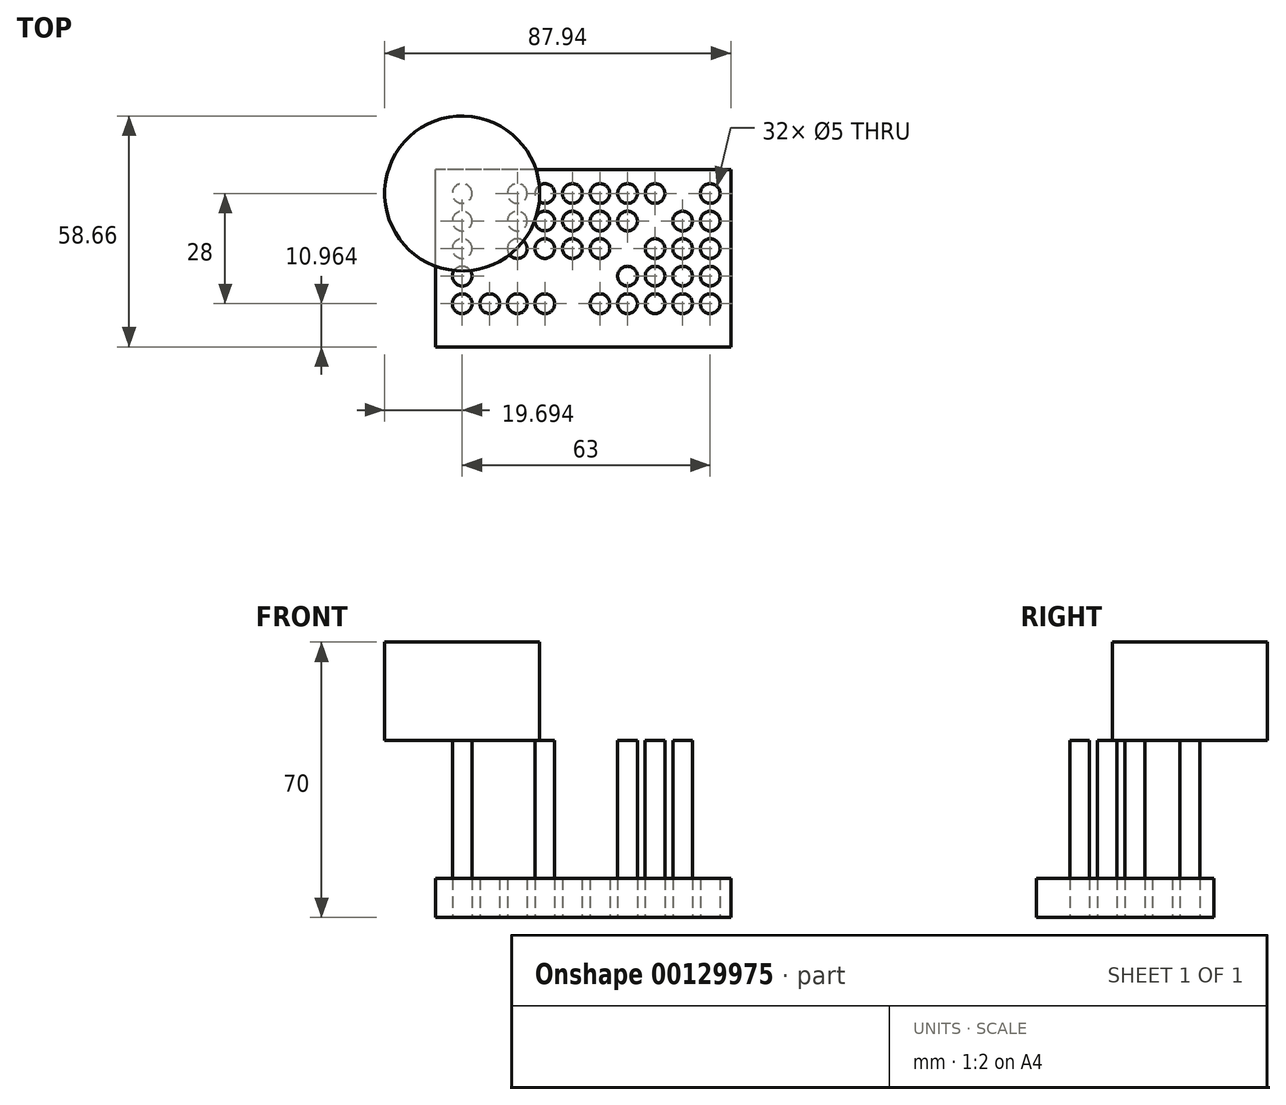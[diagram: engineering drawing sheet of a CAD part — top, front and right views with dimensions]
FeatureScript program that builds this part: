
annotation { "Feature Type Name" : "Feature", "Feature Type Description" : "" }
export const myFeature = defineFeature(function(context is Context, id is Id, definition is map)
    precondition{}
    {
        {
            var Q0;
            Q0=qCreatedBy(makeId("Top.planeOp"),FACE);
            var sketch = newSketch(context, id + "F0", { "sketchPlane" : qUnion([Q0])});
            skLineSegment(sketch, "E0.bottom", {"start": v(37.5, -22.5) * mm, "end": v(-37.5, -22.5) * mm});
            skLineSegment(sketch, "E0.top", {"start": v(37.5, 22.5) * mm, "end": v(-37.5, 22.5) * mm});
            skLineSegment(sketch, "E0.left", {"start": v(37.5, -22.5) * mm, "end": v(37.5, 22.5) * mm});
            skLineSegment(sketch, "E0.right", {"start": v(-37.5, -22.5) * mm, "end": v(-37.5, 22.5) * mm});
            skPoint(sketch, "E0.middle", {"position": v(0, 0) * mm});
            skCircle(sketch, "E1", {"center": v(-30.75, 16.46) * mm, "radius": 2.5 * mm});
            skCircle(sketch, "E2.0.1.0", {"center": v(-30.75, 9.46) * mm, "radius": 2.5 * mm});
            skCircle(sketch, "E2.0.2.0", {"center": v(-30.75, 2.46) * mm, "radius": 2.5 * mm});
            skCircle(sketch, "E2.0.3.0", {"center": v(-30.75, -4.54) * mm, "radius": 2.5 * mm});
            skCircle(sketch, "E2.0.4.0", {"center": v(-30.75, -11.54) * mm, "radius": 2.5 * mm});
            skCircle(sketch, "E2.1.0.0", {"center": v(-23.75, 16.46) * mm, "radius": 2.5 * mm});
            skCircle(sketch, "E2.1.1.0", {"center": v(-23.75, 9.46) * mm, "radius": 2.5 * mm});
            skCircle(sketch, "E2.1.2.0", {"center": v(-23.75, 2.46) * mm, "radius": 2.5 * mm});
            skCircle(sketch, "E2.1.3.0", {"center": v(-23.75, -4.54) * mm, "radius": 2.5 * mm});
            skCircle(sketch, "E2.1.4.0", {"center": v(-23.75, -11.54) * mm, "radius": 2.5 * mm});
            skCircle(sketch, "E2.2.0.0", {"center": v(-16.75, 16.46) * mm, "radius": 2.5 * mm});
            skCircle(sketch, "E2.2.1.0", {"center": v(-16.75, 9.46) * mm, "radius": 2.5 * mm});
            skCircle(sketch, "E2.2.2.0", {"center": v(-16.75, 2.46) * mm, "radius": 2.5 * mm});
            skCircle(sketch, "E2.2.3.0", {"center": v(-16.75, -4.54) * mm, "radius": 2.5 * mm});
            skCircle(sketch, "E2.2.4.0", {"center": v(-16.75, -11.54) * mm, "radius": 2.5 * mm});
            skCircle(sketch, "E2.3.0.0", {"center": v(-9.75, 16.46) * mm, "radius": 2.5 * mm});
            skCircle(sketch, "E2.3.1.0", {"center": v(-9.75, 9.46) * mm, "radius": 2.5 * mm});
            skCircle(sketch, "E2.3.2.0", {"center": v(-9.75, 2.46) * mm, "radius": 2.5 * mm});
            skCircle(sketch, "E2.3.3.0", {"center": v(-9.75, -4.54) * mm, "radius": 2.5 * mm});
            skCircle(sketch, "E2.3.4.0", {"center": v(-9.75, -11.54) * mm, "radius": 2.5 * mm});
            skCircle(sketch, "E2.4.0.0", {"center": v(-2.75, 16.46) * mm, "radius": 2.5 * mm});
            skCircle(sketch, "E2.4.1.0", {"center": v(-2.75, 9.46) * mm, "radius": 2.5 * mm});
            skCircle(sketch, "E2.4.2.0", {"center": v(-2.75, 2.46) * mm, "radius": 2.5 * mm});
            skCircle(sketch, "E2.4.3.0", {"center": v(-2.75, -4.54) * mm, "radius": 2.5 * mm});
            skCircle(sketch, "E2.4.4.0", {"center": v(-2.75, -11.54) * mm, "radius": 2.5 * mm});
            skCircle(sketch, "E2.5.0.0", {"center": v(4.25, 16.46) * mm, "radius": 2.5 * mm});
            skCircle(sketch, "E2.5.1.0", {"center": v(4.25, 9.46) * mm, "radius": 2.5 * mm});
            skCircle(sketch, "E2.5.2.0", {"center": v(4.25, 2.46) * mm, "radius": 2.5 * mm});
            skCircle(sketch, "E2.5.3.0", {"center": v(4.25, -4.54) * mm, "radius": 2.5 * mm});
            skCircle(sketch, "E2.5.4.0", {"center": v(4.25, -11.54) * mm, "radius": 2.5 * mm});
            skCircle(sketch, "E2.6.0.0", {"center": v(11.25, 16.46) * mm, "radius": 2.5 * mm});
            skCircle(sketch, "E2.6.1.0", {"center": v(11.25, 9.46) * mm, "radius": 2.5 * mm});
            skCircle(sketch, "E2.6.2.0", {"center": v(11.25, 2.46) * mm, "radius": 2.5 * mm});
            skCircle(sketch, "E2.6.3.0", {"center": v(11.25, -4.54) * mm, "radius": 2.5 * mm});
            skCircle(sketch, "E2.6.4.0", {"center": v(11.25, -11.54) * mm, "radius": 2.5 * mm});
            skCircle(sketch, "E2.7.0.0", {"center": v(18.25, 16.46) * mm, "radius": 2.5 * mm});
            skCircle(sketch, "E2.7.1.0", {"center": v(18.25, 9.46) * mm, "radius": 2.5 * mm});
            skCircle(sketch, "E2.7.2.0", {"center": v(18.25, 2.46) * mm, "radius": 2.5 * mm});
            skCircle(sketch, "E2.7.3.0", {"center": v(18.25, -4.54) * mm, "radius": 2.5 * mm});
            skCircle(sketch, "E2.7.4.0", {"center": v(18.25, -11.54) * mm, "radius": 2.5 * mm});
            skCircle(sketch, "E2.8.0.0", {"center": v(25.25, 16.46) * mm, "radius": 2.5 * mm});
            skCircle(sketch, "E2.8.1.0", {"center": v(25.25, 9.46) * mm, "radius": 2.5 * mm});
            skCircle(sketch, "E2.8.2.0", {"center": v(25.25, 2.46) * mm, "radius": 2.5 * mm});
            skCircle(sketch, "E2.8.3.0", {"center": v(25.25, -4.54) * mm, "radius": 2.5 * mm});
            skCircle(sketch, "E2.8.4.0", {"center": v(25.25, -11.54) * mm, "radius": 2.5 * mm});
            skCircle(sketch, "E2.9.0.0", {"center": v(32.25, 16.46) * mm, "radius": 2.5 * mm});
            skCircle(sketch, "E2.9.1.0", {"center": v(32.25, 9.46) * mm, "radius": 2.5 * mm});
            skCircle(sketch, "E2.9.2.0", {"center": v(32.25, 2.46) * mm, "radius": 2.5 * mm});
            skCircle(sketch, "E2.9.3.0", {"center": v(32.25, -4.54) * mm, "radius": 2.5 * mm});
            skCircle(sketch, "E2.9.4.0", {"center": v(32.25, -11.54) * mm, "radius": 2.5 * mm});
            skLineSegment(sketch, "E2.direction1", {"start": v(-30.75, 16.46) * mm, "end": v(-23.75, 16.46) * mm, "construction": true});
            skLineSegment(sketch, "E2.direction2", {"start": v(-30.75, 16.46) * mm, "end": v(-30.75, 9.46) * mm, "construction": true});
            skSolve(sketch);
        }
        {
            var Q0;
            Q0 = qSketchRegion(id + "F0", true);
            var Q1;
            Q1=makeQuery(id+"F0.imprint","IMPRINT",FACE,{"disambiguationData":[TD([[makeQuery(id+"F0.imprint","IMPRINT",EDGE,{"derivedFrom":sQuery(id+"F0.wireOp",EDGE,"E2.1.0.0")}),1.0]])]});
            var Q2;
            Q2=makeQuery(id+"F0.imprint","IMPRINT",FACE,{"disambiguationData":[TD([[makeQuery(id+"F0.imprint","IMPRINT",EDGE,{"derivedFrom":sQuery(id+"F0.wireOp",EDGE,"E2.1.1.0")}),1.0]])]});
            var Q3;
            Q3=makeQuery(id+"F0.imprint","IMPRINT",FACE,{"disambiguationData":[TD([[makeQuery(id+"F0.imprint","IMPRINT",EDGE,{"derivedFrom":sQuery(id+"F0.wireOp",EDGE,"E2.1.2.0")}),1.0]])]});
            var Q4;
            Q4=makeQuery(id+"F0.imprint","IMPRINT",FACE,{"disambiguationData":[TD([[makeQuery(id+"F0.imprint","IMPRINT",EDGE,{"derivedFrom":sQuery(id+"F0.wireOp",EDGE,"E2.1.3.0")}),1.0]])]});
            var Q5;
            Q5=makeQuery(id+"F0.imprint","IMPRINT",FACE,{"disambiguationData":[TD([[makeQuery(id+"F0.imprint","IMPRINT",EDGE,{"derivedFrom":sQuery(id+"F0.wireOp",EDGE,"E2.2.3.0")}),1.0]])]});
            var Q6;
            Q6=makeQuery(id+"F0.imprint","IMPRINT",FACE,{"disambiguationData":[TD([[makeQuery(id+"F0.imprint","IMPRINT",EDGE,{"derivedFrom":sQuery(id+"F0.wireOp",EDGE,"E2.3.3.0")}),1.0]])]});
            var Q7;
            Q7=makeQuery(id+"F0.imprint","IMPRINT",FACE,{"disambiguationData":[TD([[makeQuery(id+"F0.imprint","IMPRINT",EDGE,{"derivedFrom":sQuery(id+"F0.wireOp",EDGE,"E2.4.3.0")}),1.0]])]});
            var Q8;
            Q8=makeQuery(id+"F0.imprint","IMPRINT",FACE,{"disambiguationData":[TD([[makeQuery(id+"F0.imprint","IMPRINT",EDGE,{"derivedFrom":sQuery(id+"F0.wireOp",EDGE,"E2.4.4.0")}),1.0]])]});
            var Q9;
            Q9=makeQuery(id+"F0.imprint","IMPRINT",FACE,{"disambiguationData":[TD([[makeQuery(id+"F0.imprint","IMPRINT",EDGE,{"derivedFrom":sQuery(id+"F0.wireOp",EDGE,"E2.5.3.0")}),1.0]])]});
            var Q10;
            Q10=makeQuery(id+"F0.imprint","IMPRINT",FACE,{"disambiguationData":[TD([[makeQuery(id+"F0.imprint","IMPRINT",EDGE,{"derivedFrom":sQuery(id+"F0.wireOp",EDGE,"E2.6.2.0")}),1.0]])]});
            var Q11;
            Q11=makeQuery(id+"F0.imprint","IMPRINT",FACE,{"disambiguationData":[TD([[makeQuery(id+"F0.imprint","IMPRINT",EDGE,{"derivedFrom":sQuery(id+"F0.wireOp",EDGE,"E2.7.1.0")}),1.0]])]});
            var Q12;
            Q12=makeQuery(id+"F0.imprint","IMPRINT",FACE,{"disambiguationData":[TD([[makeQuery(id+"F0.imprint","IMPRINT",EDGE,{"derivedFrom":sQuery(id+"F0.wireOp",EDGE,"E2.8.0.0")}),1.0]])]});
            extrude(context, id + "F1", {"entities" : qUnion([Q0, Q1, Q2, Q3, Q4, Q5, Q6, Q7, Q8, Q9, Q10, Q11, Q12]), "depth" : 10 * mm});
        }
        {
            var Q0;
            Q0=makeQuery(id+"F0.imprint","IMPRINT",FACE,{"disambiguationData":[TD([[makeQuery(id+"F0.imprint","IMPRINT",EDGE,{"derivedFrom":sQuery(id+"F0.wireOp",EDGE,"E1")}),1.0]])]});
            var Q1;
            Q1=makeQuery(id+"F0.imprint","IMPRINT",FACE,{"disambiguationData":[TD([[makeQuery(id+"F0.imprint","IMPRINT",EDGE,{"derivedFrom":sQuery(id+"F0.wireOp",EDGE,"E2.3.0.0")}),1.0]])]});
            var Q2;
            Q2=makeQuery(id+"F0.imprint","IMPRINT",FACE,{"disambiguationData":[TD([[makeQuery(id+"F0.imprint","IMPRINT",EDGE,{"derivedFrom":sQuery(id+"F0.wireOp",EDGE,"E2.3.2.0")}),1.0]])]});
            var Q3;
            Q3=makeQuery(id+"F0.imprint","IMPRINT",FACE,{"disambiguationData":[TD([[makeQuery(id+"F0.imprint","IMPRINT",EDGE,{"derivedFrom":sQuery(id+"F0.wireOp",EDGE,"E2.6.3.0")}),1.0]])]});
            var Q4;
            Q4=makeQuery(id+"F0.imprint","IMPRINT",FACE,{"disambiguationData":[TD([[makeQuery(id+"F0.imprint","IMPRINT",EDGE,{"derivedFrom":sQuery(id+"F0.wireOp",EDGE,"E2.8.3.0")}),1.0]])]});
            var Q5;
            Q5=makeQuery(id+"F0.imprint","IMPRINT",FACE,{"disambiguationData":[TD([[makeQuery(id+"F0.imprint","IMPRINT",EDGE,{"derivedFrom":sQuery(id+"F0.wireOp",EDGE,"E2.7.4.0")}),1.0]])]});
            extrude(context, id + "F2", {"entities" : qUnion([Q0, Q1, Q2, Q3, Q4, Q5]), "operationType" : NewBodyOperationType.ADD, "depth" : 45 * mm});
        }
        {
            var Q0;
            Q0=makeQuery(id+"F2.opExtrude","CAP_FACE",FACE,{"disambiguationData":[OSD([sQuery(id+"F0.wireOp",EDGE,"E1")])],"isStart":false});
            var sketch = newSketch(context, id + "F3", { "sketchPlane" : qUnion([Q0])});
            skCircle(sketch, "E3", {"center": v(-30.75, 16.46) * mm, "radius": 19.7 * mm});
            skSolve(sketch);
        }
        {
            var Q0;
            Q0 = qSketchRegion(id + "F3", true);
            extrude(context, id + "F4", {"entities" : qUnion([Q0]), "operationType" : NewBodyOperationType.ADD, "depth" : 25 * mm});
        }
    });
